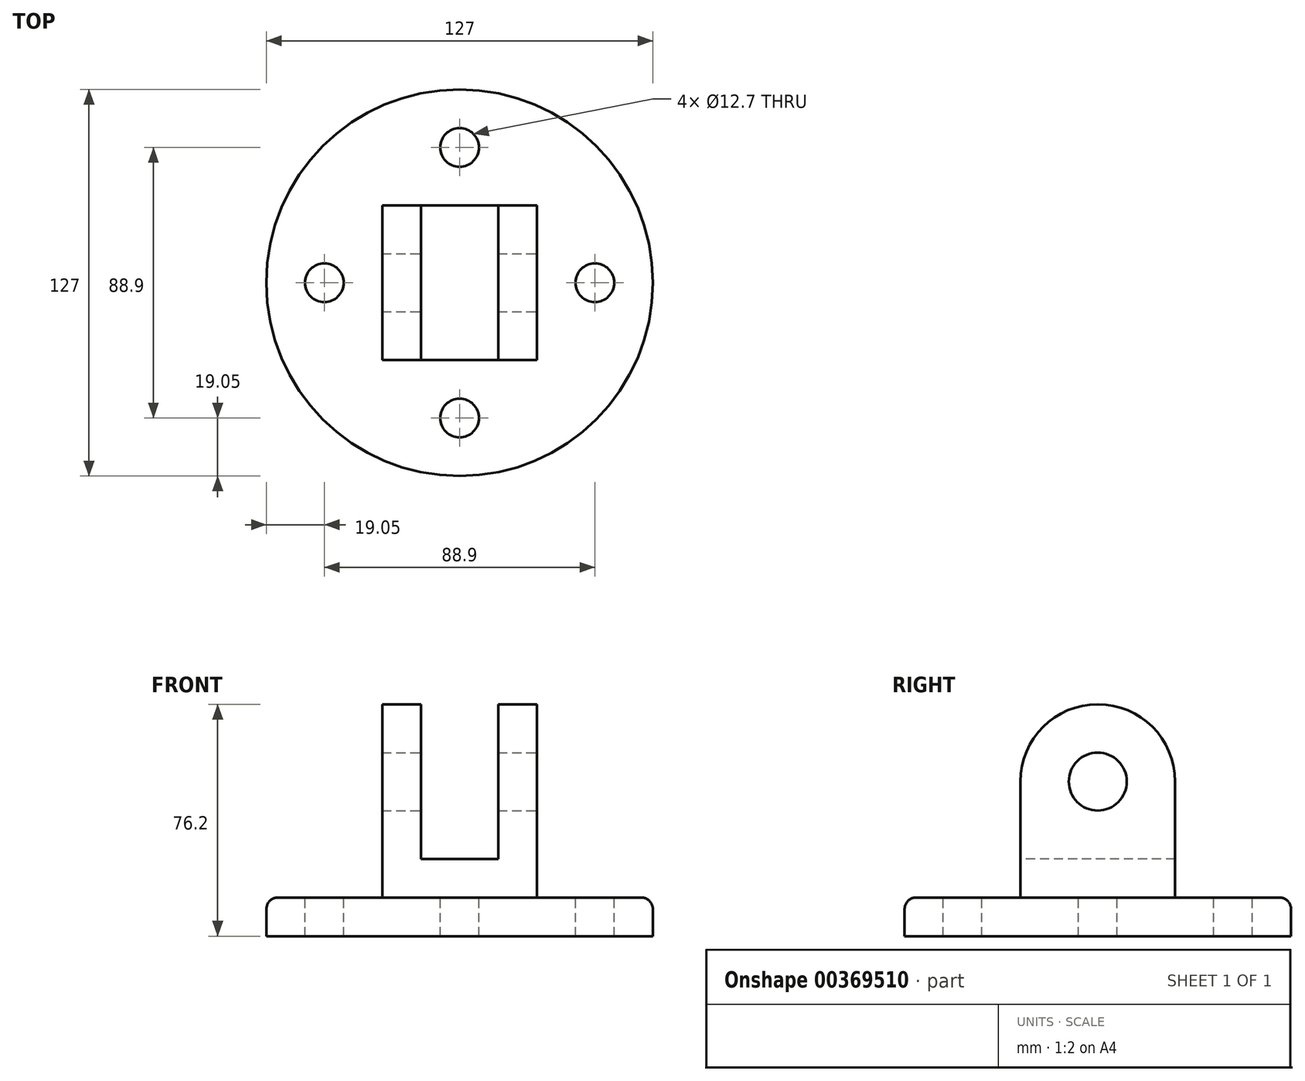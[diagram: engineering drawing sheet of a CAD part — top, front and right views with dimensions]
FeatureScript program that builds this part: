
annotation { "Feature Type Name" : "Feature", "Feature Type Description" : "" }
export const myFeature = defineFeature(function(context is Context, id is Id, definition is map)
    precondition{}
    {
        {
            var Q0;
            Q0=qCreatedBy(makeId("Top.planeOp"),FACE);
            var sketch = newSketch(context, id + "F0", { "sketchPlane" : qUnion([Q0])});
            skCircle(sketch, "E0", {"center": v(0, 0) * mm, "radius": 63.5 * mm});
            skSolve(sketch);
        }
        {
            var Q0;
            Q0=makeQuery(id+"F0.imprint","IMPRINT",FACE,{"disambiguationData":[TD([[makeQuery(id+"F0.imprint","IMPRINT",EDGE,{"derivedFrom":sQuery(id+"F0.wireOp",EDGE,"E0")}),1.0]])]});
            extrude(context, id + "F1", {"entities" : qUnion([Q0]), "depth" : 12.7 * mm});
        }
        {
            var Q0;
            Q0=makeQuery(id+"F1.opExtrude","CAP_FACE",FACE,{"disambiguationData":[OSD([sQuery(id+"F0.wireOp",EDGE,"E0")])],"isStart":false});
            var sketch = newSketch(context, id + "F2", { "sketchPlane" : qUnion([Q0])});
            skCircle(sketch, "E1", {"center": v(0, 0) * mm, "radius": 44.45 * mm});
            skCircle(sketch, "E2", {"center": v(0, 44.45) * mm, "radius": 6.35 * mm});
            skCircle(sketch, "E3", {"center": v(-44.45, 0) * mm, "radius": 6.35 * mm});
            skCircle(sketch, "E4", {"center": v(0, -44.45) * mm, "radius": 6.35 * mm});
            skCircle(sketch, "E5", {"center": v(44.45, 0) * mm, "radius": 6.35 * mm});
            skSolve(sketch);
        }
        {
            var Q0;
            {var subQ0=sQuery(id+"F2.wireOp",EDGE,"E2");var subQ1=sQuery(id+"F2.wireOp",EDGE,"E1");var subQ2=makeQuery(id+"F2.imprint","INTERSECT",VERTEX,{"disambiguationData":[OD(0.0)],"derivedFrom":[subQ1,subQ0]});Q0=makeQuery(id+"F2.imprint","IMPRINT",FACE,{"disambiguationData":[TD([[makeQuery(id+"F2.imprint","IMPRINT",EDGE,{"disambiguationData":[TD([[subQ2,-1.0]])],"derivedFrom":subQ1}),-1.0]])]});}
            var Q1;
            {var subQ0=sQuery(id+"F2.wireOp",EDGE,"E2");var subQ1=sQuery(id+"F2.wireOp",EDGE,"E1");var subQ2=makeQuery(id+"F2.imprint","INTERSECT",VERTEX,{"disambiguationData":[OD(0.0)],"derivedFrom":[subQ1,subQ0]});Q1=makeQuery(id+"F2.imprint","IMPRINT",FACE,{"disambiguationData":[TD([[makeQuery(id+"F2.imprint","IMPRINT",EDGE,{"disambiguationData":[TD([[subQ2,-1.0]])],"derivedFrom":subQ1}),1.0]])]});}
            var Q2;
            {var subQ0=sQuery(id+"F2.wireOp",EDGE,"E3");var subQ1=sQuery(id+"F2.wireOp",EDGE,"E1");var subQ2=makeQuery(id+"F2.imprint","INTERSECT",VERTEX,{"disambiguationData":[OD(0.0)],"derivedFrom":[subQ1,subQ0]});Q2=makeQuery(id+"F2.imprint","IMPRINT",FACE,{"disambiguationData":[TD([[makeQuery(id+"F2.imprint","IMPRINT",EDGE,{"disambiguationData":[TD([[subQ2,-1.0]])],"derivedFrom":subQ1}),1.0]])]});}
            var Q3;
            {var subQ0=sQuery(id+"F2.wireOp",EDGE,"E3");var subQ1=sQuery(id+"F2.wireOp",EDGE,"E1");var subQ2=makeQuery(id+"F2.imprint","INTERSECT",VERTEX,{"disambiguationData":[OD(0.0)],"derivedFrom":[subQ1,subQ0]});Q3=makeQuery(id+"F2.imprint","IMPRINT",FACE,{"disambiguationData":[TD([[makeQuery(id+"F2.imprint","IMPRINT",EDGE,{"disambiguationData":[TD([[subQ2,-1.0]])],"derivedFrom":subQ1}),-1.0]])]});}
            var Q4;
            {var subQ0=sQuery(id+"F2.wireOp",EDGE,"E4");var subQ1=sQuery(id+"F2.wireOp",EDGE,"E1");var subQ2=makeQuery(id+"F2.imprint","INTERSECT",VERTEX,{"disambiguationData":[OD(0.0)],"derivedFrom":[subQ1,subQ0]});Q4=makeQuery(id+"F2.imprint","IMPRINT",FACE,{"disambiguationData":[TD([[makeQuery(id+"F2.imprint","IMPRINT",EDGE,{"disambiguationData":[TD([[subQ2,-1.0]])],"derivedFrom":subQ1}),-1.0]])]});}
            var Q5;
            {var subQ0=sQuery(id+"F2.wireOp",EDGE,"E4");var subQ1=sQuery(id+"F2.wireOp",EDGE,"E1");var subQ2=makeQuery(id+"F2.imprint","INTERSECT",VERTEX,{"disambiguationData":[OD(0.0)],"derivedFrom":[subQ1,subQ0]});Q5=makeQuery(id+"F2.imprint","IMPRINT",FACE,{"disambiguationData":[TD([[makeQuery(id+"F2.imprint","IMPRINT",EDGE,{"disambiguationData":[TD([[subQ2,-1.0]])],"derivedFrom":subQ1}),1.0]])]});}
            var Q6;
            {var subQ0=sQuery(id+"F2.wireOp",EDGE,"E5");var subQ1=sQuery(id+"F2.wireOp",EDGE,"E1");var subQ2=makeQuery(id+"F2.imprint","INTERSECT",VERTEX,{"disambiguationData":[OD(0.0)],"derivedFrom":[subQ1,subQ0]});Q6=makeQuery(id+"F2.imprint","IMPRINT",FACE,{"disambiguationData":[TD([[makeQuery(id+"F2.imprint","IMPRINT",EDGE,{"disambiguationData":[TD([[subQ2,1.0]])],"derivedFrom":subQ1}),1.0]])]});}
            var Q7;
            {var subQ0=sQuery(id+"F2.wireOp",EDGE,"E5");var subQ1=sQuery(id+"F2.wireOp",EDGE,"E1");var subQ2=makeQuery(id+"F2.imprint","INTERSECT",VERTEX,{"disambiguationData":[OD(0.0)],"derivedFrom":[subQ1,subQ0]});Q7=makeQuery(id+"F2.imprint","IMPRINT",FACE,{"disambiguationData":[TD([[makeQuery(id+"F2.imprint","IMPRINT",EDGE,{"disambiguationData":[TD([[subQ2,1.0]])],"derivedFrom":subQ1}),-1.0]])]});}
            extrude(context, id + "F3", {"entities" : qUnion([Q0, Q1, Q2, Q3, Q4, Q5, Q6, Q7]), "operationType" : NewBodyOperationType.REMOVE, "endBound" : BoundingType.THROUGH_ALL, "oppositeDirection" : true, "depth" : 25.4 * mm});
        }
        {
            var Q0;
            Q0=makeQuery(id+"F1.opExtrude","CAP_FACE",FACE,{"disambiguationData":[OSD([sQuery(id+"F0.wireOp",EDGE,"E0")])],"isStart":false});
            var sketch = newSketch(context, id + "F4", { "sketchPlane" : qUnion([Q0])});
            skLineSegment(sketch, "E6.bottom", {"start": v(25.4, -25.4) * mm, "end": v(-25.4, -25.4) * mm});
            skLineSegment(sketch, "E6.top", {"start": v(25.4, 25.4) * mm, "end": v(-25.4, 25.4) * mm});
            skLineSegment(sketch, "E6.left", {"start": v(25.4, -25.4) * mm, "end": v(25.4, 25.4) * mm});
            skLineSegment(sketch, "E6.right", {"start": v(-25.4, -25.4) * mm, "end": v(-25.4, 25.4) * mm});
            skPoint(sketch, "E6.middle", {"position": v(0, 0) * mm});
            skSolve(sketch);
        }
        {
            var Q0;
            Q0 = qSketchRegion(id + "F4", true);
            extrude(context, id + "F5", {"entities" : qUnion([Q0]), "operationType" : NewBodyOperationType.ADD, "depth" : 63.5 * mm});
        }
        {
            var Q0;
            Q0=makeQuery(id+"F5.opExtrude","SWEPT_FACE",FACE,{"disambiguationData":[OSD([sQuery(id+"F4.wireOp",EDGE,"E6.left")])]});
            var sketch = newSketch(context, id + "F6", { "sketchPlane" : qUnion([Q0])});
            skCircle(sketch, "E7", {"center": v(0, 50.8) * mm, "radius": 9.53 * mm});
            skLineSegment(sketch, "E8", {"start": v(-25.4, 50.8) * mm, "end": v(-25.4, 12.7) * mm});
            skLineSegment(sketch, "E9", {"start": v(25.4, 50.8) * mm, "end": v(25.4, 12.7) * mm});
            skArc(sketch, "E10", {"start": v(25.4, 50.8) * mm, "mid": v(0, 76.2) * mm, "end": v(-25.4, 50.8) * mm});
            skSolve(sketch);
        }
        {
            var Q0;
            {var subQ0=sQuery(id+"F6.wireOp",EDGE,"E10");var subQ1=sQuery(id+"F4.wireOp",EDGE,"E6.left");var subQ4=makeQuery(id+"F5.opExtrude","CAP_EDGE",EDGE,{"disambiguationData":[OSD([subQ1])],"isStart":false});var subQ5=makeQuery(id+"F6.imprint","INTERSECT",VERTEX,{"derivedFrom":[subQ4,subQ0]});Q0=makeQuery(id+"F6.imprint","IMPRINT",FACE,{"disambiguationData":[TD([[makeQuery(id+"F6.imprint","IMPRINT",EDGE,{"disambiguationData":[TD([[subQ5,1.0]])],"derivedFrom":subQ4}),-1.0]])]});}
            var Q1;
            {var subQ0=sQuery(id+"F6.wireOp",EDGE,"E10");var subQ1=sQuery(id+"F4.wireOp",EDGE,"E6.left");var subQ4=makeQuery(id+"F5.opExtrude","CAP_EDGE",EDGE,{"disambiguationData":[OSD([subQ1])],"isStart":false});var subQ5=makeQuery(id+"F6.imprint","INTERSECT",VERTEX,{"derivedFrom":[subQ4,subQ0]});Q1=makeQuery(id+"F6.imprint","IMPRINT",FACE,{"disambiguationData":[TD([[makeQuery(id+"F6.imprint","IMPRINT",EDGE,{"disambiguationData":[TD([[subQ5,-1.0]])],"derivedFrom":subQ4}),-1.0]])]});}
            var Q2;
            Q2=makeQuery(id+"F6.imprint","IMPRINT",FACE,{"disambiguationData":[TD([[makeQuery(id+"F6.imprint","IMPRINT",EDGE,{"derivedFrom":sQuery(id+"F6.wireOp",EDGE,"E7")}),1.0]])]});
            extrude(context, id + "F7", {"entities" : qUnion([Q0, Q1, Q2]), "operationType" : NewBodyOperationType.REMOVE, "endBound" : BoundingType.THROUGH_ALL, "oppositeDirection" : true, "depth" : 25.4 * mm});
        }
        {
            var Q0;
            Q0=makeQuery(id+"F5.opExtrude","SWEPT_FACE",FACE,{"disambiguationData":[OSD([sQuery(id+"F4.wireOp",EDGE,"E6.bottom")])]});
            var sketch = newSketch(context, id + "F8", { "sketchPlane" : qUnion([Q0])});
            skLineSegment(sketch, "E11.bottom", {"start": v(12.7, 25.4) * mm, "end": v(-12.7, 25.4) * mm});
            skLineSegment(sketch, "E11.top", {"start": v(12.7, 76.2) * mm, "end": v(-12.7, 76.2) * mm});
            skLineSegment(sketch, "E11.left", {"start": v(12.7, 25.4) * mm, "end": v(12.7, 76.2) * mm});
            skLineSegment(sketch, "E11.right", {"start": v(-12.7, 25.4) * mm, "end": v(-12.7, 76.2) * mm});
            skPoint(sketch, "E11.middle", {"position": v(0, 50.8) * mm});
            skSolve(sketch);
        }
        {
            var Q0;
            {var subQ0=sQuery(id+"F8.wireOp",EDGE,"E11.bottom");Q0=makeQuery(id+"F8.imprint","IMPRINT",FACE,{"disambiguationData":[TD([[makeQuery(id+"F8.imprint","IMPRINT",EDGE,{"derivedFrom":subQ0}),-1.0]])]});}
            var Q1;
            {var subQ0=sQuery(id+"F8.wireOp",EDGE,"E11.top");Q1=makeQuery(id+"F8.imprint","IMPRINT",FACE,{"disambiguationData":[TD([[makeQuery(id+"F8.imprint","IMPRINT",EDGE,{"derivedFrom":subQ0}),1.0]])]});}
            extrude(context, id + "F9", {"entities" : qUnion([Q0, Q1]), "operationType" : NewBodyOperationType.REMOVE, "endBound" : BoundingType.THROUGH_ALL, "oppositeDirection" : true, "depth" : 25.4 * mm});
        }
        {
            var Q0;
            Q0=makeQuery(id+"F1.opExtrude","CAP_EDGE",EDGE,{"disambiguationData":[OSD([sQuery(id+"F0.wireOp",EDGE,"E0")])],"isStart":false});
            fillet(context, id + "F10", {"entities" : qUnion([Q0]), "radius" : 3.8 * mm, "tangentPropagation" : true, "allowEdgeOverflow" : false});
        }
    });
